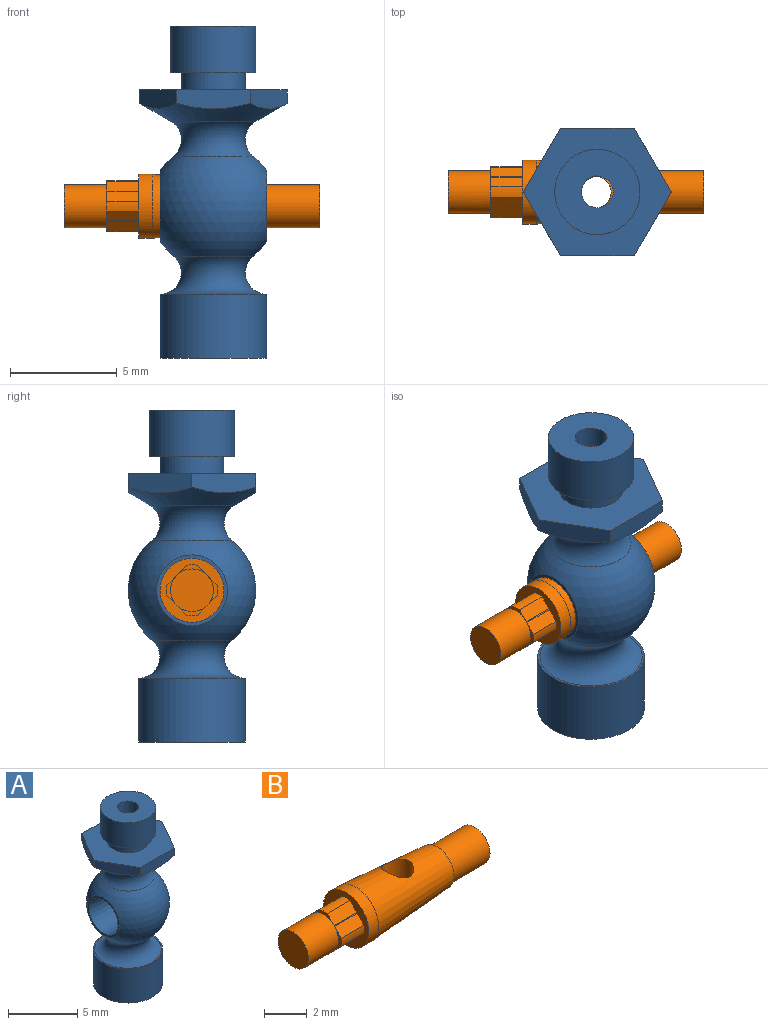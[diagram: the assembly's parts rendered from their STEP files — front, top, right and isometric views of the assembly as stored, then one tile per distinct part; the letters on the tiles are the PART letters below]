
ASSEMBLY  parts=2 mates=1
PART A: 23 faces, bbox 8x8x16.6 mm
  f0: plane 6.93x6mm, normal (0,0,1), area 24.1mm2, adj f7,f17,f18,f19,f20,f21,f22
  f1: cone r=2mm half-angle=60deg, axis (0,0,1), area 29mm2, adj f8,f17,f18,f19,f20,f21,f22
  f2: cone r=1.12mm half-angle=4deg, axis (-1,0,0), area 37.5mm2, adj f13,f14,f15,f16
  f3: sphere r=3mm, area 69.4mm2, adj f8,f9,f13,f14
  f4: plane 4x4mm, normal (0,0,1), area 10.8mm2, adj f5,f15
  f5: cylinder r=2mm len=4mm, axis (0,0,1), area 27.6mm2, adj f4,f6
  f6: plane 4x4mm, normal (0,0,-1), area 5.5mm2, adj f5,f7
  f7: cylinder r=1.5mm len=3mm, axis (0,0,1), area 7.5mm2, adj f0,f6
  f8: torus R=2.5mm, axis (0,0,1), area 20.2mm2, adj f1,f3
  f9: torus R=2.5mm, axis (0,0,1), area 26mm2, adj f3,f10
  f10: plane 5x5mm, normal (0,0,1), area 1.5mm2, adj f9,f11
  f11: cylinder r=2.5mm len=5mm, axis (0,0,1), area 47.1mm2, adj f10,f12
  f12: plane 5x5mm, normal (0,0,-1), area 17.9mm2, adj f11,f16
  f13: plane 3.32x3.32mm, normal (1,0,0), area 4.6mm2, adj f2,f3
  f14: plane 3.32x3.32mm, normal (-1,0,0), area 1.7mm2, adj f2,f3
  f15: cylinder r=0.75mm len=7.23mm, axis (0,0,-1), area 33.8mm2, adj f2,f4
  f16: cylinder r=0.75mm len=5.89mm, axis (0,0,-1), area 27.5mm2, adj f2,f12
  f17: plane 4.55x1.96mm, normal (0,1,0), area 2.8mm2, adj f0,f1,f18,f22
  f18: plane 4.07x2.8mm, normal (0.87,0.5,0), area 2.8mm2, adj f0,f1,f17,f19
  f19: plane 4.07x2.8mm, normal (0.87,-0.5,0), area 2.8mm2, adj f0,f1,f18,f20
  f20: plane 4.55x1.96mm, normal (0,-1,0), area 2.8mm2, adj f0,f1,f19,f21
  f21: plane 4.07x2.8mm, normal (-0.87,-0.5,0), area 2.8mm2, adj f0,f1,f20,f22
  f22: plane 4.07x2.8mm, normal (-0.87,0.5,0), area 2.8mm2, adj f0,f1,f17,f21
PART B: 25 faces, bbox 12x3x3 mm
  f0: cylinder r=1.2mm len=1.5mm, axis (-1,0,0), area 0.7mm2, adj f4,f12,f18,f23
  f1: cylinder r=1.2mm len=1.5mm, axis (-1,0,0), area 0.8mm2, adj f5,f12,f21,f24
  f2: cylinder r=1.2mm len=1.5mm, axis (-1,0,0), area 0.7mm2, adj f6,f12,f19,f22
  f3: cylinder r=1.2mm len=1.5mm, axis (-1,0,0), area 0.8mm2, adj f12,f13,f17,f20
  f4: plane 1.36x0.47mm, normal (-1,0,0), area 0.2mm2, adj f0,f14,f18,f23
  f5: plane 1.4x0.48mm, normal (-1,0,0), area 0.2mm2, adj f1,f14,f21,f24
  f6: plane 1.36x0.47mm, normal (-1,0,0), area 0.2mm2, adj f2,f14,f19,f22
  f7: cone r=1.12mm half-angle=4deg, axis (-1,0,0), area 40.6mm2, adj f10,f11,f16
  f8: plane 2x2mm, normal (1,0,0), area 3.1mm2, adj f9
  f9: cylinder r=1mm len=2.5mm, axis (-1,0,0), area 15.7mm2, adj f8,f10
  f10: plane 2.25x2.25mm, normal (1,0,0), area 0.8mm2, adj f7,f9
  f11: cylinder r=1.5mm len=3mm, axis (-1,0,0), area 6mm2, adj f7,f12
  f12: plane 3x3mm, normal (-1,0,0), area 3.3mm2, adj f0,f1,f2,f3,f11,f14,f17,f18
  f13: plane 1.4x0.48mm, normal (-1,0,0), area 0.2mm2, adj f3,f14,f17,f20
  f14: cylinder r=1mm len=3.5mm, axis (-1,0,0), area 12.8mm2, adj f4,f5,f6,f12,f13,f15,f17,f18
  f15: plane 2x2mm, normal (-1,0,0), area 3.1mm2, adj f14
  f16: cylinder r=0.75mm len=2.72mm, axis (0,0,-1), area 11.2mm2, adj f7
  f17: plane 1.5x0.46mm, normal (0,0.72,0.7), area 1mm2, adj f3,f12,f13,f14
  f18: plane 1.5x0.46mm, normal (0,0.72,0.7), area 1mm2, adj f0,f4,f12,f14
  f19: plane 1.5x0.46mm, normal (0,-0.72,0.7), area 1mm2, adj f2,f6,f12,f14
  f20: plane 1.5x0.46mm, normal (0,-0.72,0.7), area 1mm2, adj f3,f12,f13,f14
  f21: plane 1.5x0.46mm, normal (0,-0.72,-0.7), area 1mm2, adj f1,f5,f12,f14
  f22: plane 1.5x0.46mm, normal (0,-0.72,-0.7), area 1mm2, adj f2,f6,f12,f14
  f23: plane 1.5x0.46mm, normal (0,0.72,-0.7), area 1mm2, adj f0,f4,f12,f14
  f24: plane 1.5x0.46mm, normal (0,0.72,-0.7), area 1mm2, adj f1,f5,f12,f14
PLACE A at identity
PLACE B t=(-0.1,0,0)mm
MATE revolute B.f0 <-> A.f2  axis (-1,0,0) through (2.5,0,0)mm
